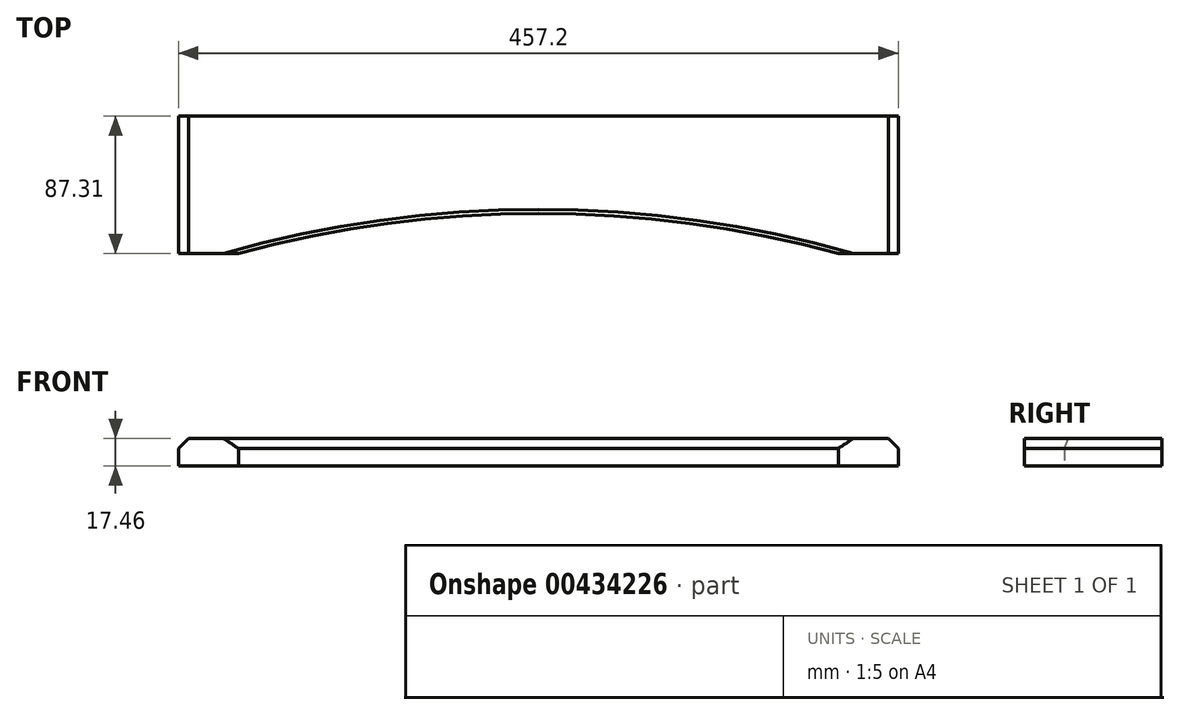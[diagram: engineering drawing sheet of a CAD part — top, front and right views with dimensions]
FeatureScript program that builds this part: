
annotation { "Feature Type Name" : "Feature", "Feature Type Description" : "" }
export const myFeature = defineFeature(function(context is Context, id is Id, definition is map)
    precondition{}
    {
        {
            var Q0;
            Q0=qCreatedBy(makeId("Top.planeOp"),FACE);
            var sketch = newSketch(context, id + "F0", { "sketchPlane" : qUnion([Q0])});
            skLineSegment(sketch, "E0.bottom", {"start": v(0, 0) * mm, "end": v(38.1, 0) * mm});
            skLineSegment(sketch, "E0.top", {"start": v(0, 87.31) * mm, "end": v(457.2, 87.31) * mm});
            skLineSegment(sketch, "E0.left", {"start": v(0, 0) * mm, "end": v(0, 87.31) * mm});
            skLineSegment(sketch, "E0.right", {"start": v(457.2, 0) * mm, "end": v(457.2, 87.31) * mm});
            skLineSegment(sketch, "E1", {"start": v(38.1, 16.63) * mm, "end": v(38.1, -30.86) * mm, "construction": true});
            skLineSegment(sketch, "E2", {"start": v(419.1, 20.9) * mm, "end": v(419.1, -35.43) * mm, "construction": true});
            skLineSegment(sketch, "E3", {"start": v(38.1, 0) * mm, "end": v(419.1, 0) * mm, "construction": true});
            skLineSegment(sketch, "E4", {"start": v(419.1, 0) * mm, "end": v(457.2, 0) * mm});
            skLineSegment(sketch, "E5", {"start": v(228.6, 0) * mm, "end": v(228.6, 25.4) * mm, "construction": true});
            skArc(sketch, "E6", {"start": v(419.1, 0) * mm, "mid": v(228.6, 25.4) * mm, "end": v(38.1, 0) * mm});
            skSolve(sketch);
        }
        {
            var Q0;
            Q0 = qSketchRegion(id + "F0", true);
            extrude(context, id + "F1", {"entities" : qUnion([Q0]), "depth" : 17.46 * mm});
        }
        {
            var Q0;
            Q0=makeQuery(id+"F1.opExtrude","CAP_EDGE",EDGE,{"disambiguationData":[OSD([sQuery(id+"F0.wireOp",EDGE,"E0.left")])],"isStart":false});
            var Q1;
            Q1=makeQuery(id+"F1.opExtrude","CAP_EDGE",EDGE,{"disambiguationData":[OSD([sQuery(id+"F0.wireOp",EDGE,"E0.right")])],"isStart":false});
            chamfer(context, id + "F2", {"entities" : qUnion([Q0, Q1]), "width" : 6.35 * mm, "tangentPropagation" : true});
        }
        {
            var Q0;
            Q0=makeQuery(id+"F1.opExtrude","CAP_EDGE",EDGE,{"disambiguationData":[OSD([sQuery(id+"F0.wireOp",EDGE,"E6")])],"isStart":false});
            chamfer(context, id + "F3", {"entities" : qUnion([Q0]), "chamferType" : ChamferType.TWO_OFFSETS, "width1" : 6.35 * mm, "oppositeDirection" : false, "width2" : 2.54 * mm, "tangentPropagation" : true});
        }
    });
